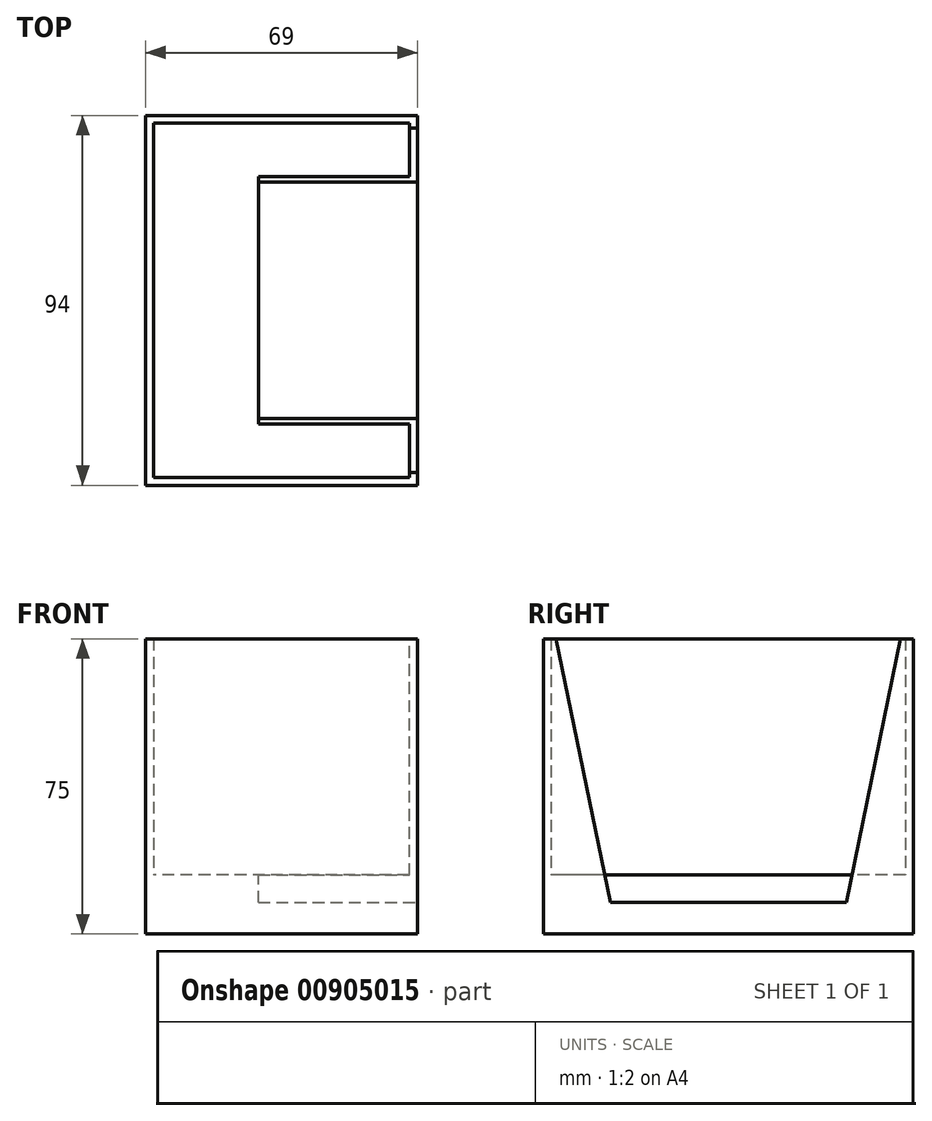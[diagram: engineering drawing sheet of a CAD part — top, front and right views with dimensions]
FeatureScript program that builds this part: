
annotation { "Feature Type Name" : "Feature", "Feature Type Description" : "" }
export const myFeature = defineFeature(function(context is Context, id is Id, definition is map)
    precondition{}
    {
        {
            var Q0;
            Q0=qCreatedBy(makeId("Top.planeOp"),FACE);
            var sketch = newSketch(context, id + "F0", { "sketchPlane" : qUnion([Q0])});
            skLineSegment(sketch, "E0.bottom", {"start": v(32.5, 45) * mm, "end": v(-32.5, 45) * mm});
            skLineSegment(sketch, "E0.top", {"start": v(32.5, -45) * mm, "end": v(-32.5, -45) * mm});
            skLineSegment(sketch, "E0.left", {"start": v(32.5, 45) * mm, "end": v(32.5, -45) * mm});
            skLineSegment(sketch, "E0.right", {"start": v(-32.5, 45) * mm, "end": v(-32.5, -45) * mm});
            skPoint(sketch, "E0.middle", {"position": v(0, 0) * mm});
            skLineSegment(sketch, "E1.0", {"start": v(34.5, 47) * mm, "end": v(-34.5, 47) * mm});
            skLineSegment(sketch, "E1.1", {"start": v(34.5, 47) * mm, "end": v(34.5, -47) * mm});
            skLineSegment(sketch, "E1.2", {"start": v(34.5, -47) * mm, "end": v(-34.5, -47) * mm});
            skLineSegment(sketch, "E1.3", {"start": v(-34.5, 47) * mm, "end": v(-34.5, -47) * mm});
            skSolve(sketch);
        }
        {
            var Q0;
            Q0 = qSketchRegion(id + "F0", true);
            extrude(context, id + "F1", {"entities" : qUnion([Q0]), "depth" : 60 * mm, "offsetDistance" : 25 * mm});
        }
        {
            var Q0;
            Q0=makeQuery(id+"F1.opExtrude","CAP_FACE",FACE,{"disambiguationData":[OSD([sQuery(id+"F0.wireOp",EDGE,"E0.bottom"),sQuery(id+"F0.wireOp",EDGE,"E0.top"),sQuery(id+"F0.wireOp",EDGE,"E0.left"),sQuery(id+"F0.wireOp",EDGE,"E0.right"),sQuery(id+"F0.wireOp",EDGE,"E1.0"),sQuery(id+"F0.wireOp",EDGE,"E1.1"),sQuery(id+"F0.wireOp",EDGE,"E1.2"),sQuery(id+"F0.wireOp",EDGE,"E1.3")])],"isStart":true});
            var sketch = newSketch(context, id + "F2", { "sketchPlane" : qUnion([Q0])});
            skLineSegment(sketch, "E2.0", {"start": v(-34.5, -47) * mm, "end": v(-34.5, 47) * mm});
            skLineSegment(sketch, "E2.1", {"start": v(34.5, -47) * mm, "end": v(-34.5, -47) * mm});
            skLineSegment(sketch, "E2.2", {"start": v(34.5, -47) * mm, "end": v(34.5, 47) * mm});
            skLineSegment(sketch, "E2.3", {"start": v(34.5, 47) * mm, "end": v(-34.5, 47) * mm});
            skSolve(sketch);
        }
        {
            var Q0;
            Q0 = qSketchRegion(id + "F2", true);
            extrude(context, id + "F3", {"entities" : qUnion([Q0]), "operationType" : NewBodyOperationType.ADD, "depth" : 15 * mm, "offsetDistance" : 25 * mm});
        }
        {
            var Q0;
            Q0=makeQuery(id+"F3.boolean.opBoolean","MERGE",FACE,{"derivedFrom":[makeQuery(id+"F1.opExtrude","SWEPT_FACE",FACE,{"disambiguationData":[OSD([sQuery(id+"F0.wireOp",EDGE,"E1.1")])]}),makeQuery(id+"F3.opExtrude","SWEPT_FACE",FACE,{"disambiguationData":[OSD([sQuery(id+"F2.wireOp",EDGE,"E2.2")])]})]});
            var sketch = newSketch(context, id + "F4", { "sketchPlane" : qUnion([Q0])});
            skLineSegment(sketch, "E3", {"start": v(0, 0) * mm, "end": v(0, 28.24) * mm, "construction": true});
            skLineSegment(sketch, "E4", {"start": v(0, -7) * mm, "end": v(30, -7) * mm});
            skLineSegment(sketch, "E5", {"start": v(30, -7) * mm, "end": v(45, 66) * mm});
            skLineSegment(sketch, "E6", {"start": v(45, 66) * mm, "end": v(0, 66) * mm});
            skLineSegment(sketch, "E7.MirrorCS", {"start": v(-45, 66) * mm, "end": v(0, 66) * mm});
            skLineSegment(sketch, "E8.MirrorCS", {"start": v(-30, -7) * mm, "end": v(-45, 66) * mm});
            skLineSegment(sketch, "E9.MirrorCS", {"start": v(0, -7) * mm, "end": v(-30, -7) * mm});
            skSolve(sketch);
        }
        {
            var Q0;
            Q0 = qSketchRegion(id + "F4", true);
            extrude(context, id + "F5", {"entities" : qUnion([Q0]), "operationType" : NewBodyOperationType.REMOVE, "oppositeDirection" : true, "depth" : 40.4 * mm, "offsetDistance" : 25 * mm});
        }
    });
